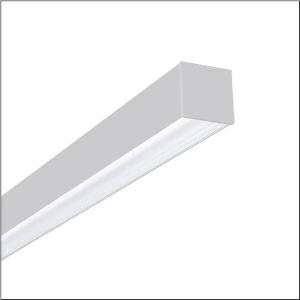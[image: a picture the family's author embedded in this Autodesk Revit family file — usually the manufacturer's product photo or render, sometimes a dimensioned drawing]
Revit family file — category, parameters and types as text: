
# Revit family: silica_r_5mx22wd1w4a_c31c
name_source: partatom
category: Lighting Fixtures
units: mm (PartAtom-declared; Revit-internal decimal feet)

## family parameters
Cut with Voids When Loaded = No
Host = Face
Light Source = No
Part Type = Normal
Room Calculation Point = No
Round Connector Dimension = Use Diameter
Shared = No

## types (1)
- --- (1 x LED, 4680 lm, 29.3 W, 4000K)
    Apparent Load = 29 VA
    CIE Flux Codes = 70 95 99 100 100
    Color Rendering = 80
    Color Temperature = 4000K
    Default Elevation = 1800 mm
    Description = Silica®, office luminaire, primary light control with wallwasher, of aluminium, light emission: direct distribution, primary light characteristic: asymmetric, installation type: surface-mounted, LED, rated luminous flux: 4.680lm, luminous efficacy: 160lm/W, light colour: 840, colour temperature: 4000K, control gear: ECG DALI, with terminal, 3+2-pole, max. 2.5mm², mains connection: 230V, AC, 50/60Hz, rated input power: 29W, luminaire housing, of aluminium, traffic white (RAL 9016), length: 1.442mm, width: 65mm, height: 64mm, protection rating (complete): IP20, insulation class (complete): insulation class I (protective earthing), certification: CE, permissible operating ambient temperature: 0..+35°C, standard: EN 50419, packaging unit: 1 piece
    Height = 64 mm
    Lamp = 1 x LED
    Lamp Light Flux = 4680 lm
    Lamp Power = 29.3 W
    Lamp count = 1
    Length = 1442 mm
    Luminous efficacy = 160 lm/W
    Manufacturer = Siteco
    ModVariant = No
    Model = 5MX22WD1W4A
    Mounting Place = Ceiling
    Mounting Type = Surface mounted
    Number of Poles = 1
    OnlyDefault = Yes
    Power Factor = 1
    Product Name = Silica®
    Product group = office luminaire | ceiling mounted
    ProductGroupID = 300
    Protection Class = Protection class I
    Protection Degree = IP 20
    RLX_Detail_Level = 1
    RLX_Emergency_Light_Flux = 0 lm
    RLX_Emergency_Type = 0
    RLX_Emergency_Type_DB = No
    RlxData = <blob elided: 23997 chars, md5=a4a08fdf>
    Socket = socket
    Standby Power = 0 W
    System Light Flux = 4680 lm
    System Power = 29 W
    Type Comments = factory setting: luminous flux: 100 % | dim-lin: 254 | 164 mA
    Type Image = l_1003937.jpg
    URL = http://relux.com
    VarID = @adj_155130
    Voltage = 0 V
    Weight = 0.00 kg
    Width = 66 mm

## geometry (parser evidence)
native form markers: Blend x4, Sweep x11
no freeform markers — native parametric forms only
